# Revit family: SystemSchroeders_2flg.Tür
name_source: partatom
category: Türen
revit_build: Autodesk Revit 2018 (Build: 20170223_1515(x64)
units: mm (PartAtom-declared; Revit-internal decimal feet)

## family parameters
Basisbauteil = Wand
Beim Laden mit Abzugskörper schneiden = Nein
Gemeinsam genutzt = Nein
Immer vertikal = Ja
OmniClass-Nummer = 23.30.10.00
OmniClass-Titel = Doors
Raumberechnungspunkt = Nein

## types (11) — shared parameters
Analytische Konstruktion = <None>
Breite = 2000 mm
Breite Rahmen Sichtfenster = 55 mm
Breite Sichtfenster = 260 mm
Dicke = 69 mm  [stored 0.226378 ft]
Einbauhöhe Sichtfenster = 1500 mm  [stored 4.92126 ft]
FrameCompensate = Edelstahl
Funktion = Innen
Hbl = 260 mm
Hersteller = System Schröders
Höhe = 2000 mm
Höhe Sichtfenster = 260 mm
Höhe Türgriff = 1050 mm
Luftdichtigkeit = bis Klasse 3 (600 Pa)
PanelWidth = 1957 mm
Rahmenbreite = 22 mm
URL = https://www.system-schroeders.de
Wandabschluss = Nach Basisbauteil
Werkstoff Griff = Edelstahl
Werkstoff Rahmen = Edelstahl
Werkstoff Rahmen Sichtfenster = Edelstahl
Werkstoff Sichtfenster = Glas
Werkstoff Türblatt = Edelstahl
Wp_left = 979 mm
Wp_right = 974 mm
Öffnungswinkel = 90.00°

## per-type parameters (varying)
| type | Druck- / Sogwiderstand | Einbruchschutz | Feuerschutz | Rauchschutz | Schallschutz | Schlagregendichtheit | Widerstandsfähigkeit gegen Winlast |
| TSN-2 | 3800Pa | RC4 RC3 RC2 RC1 | T-30 | RS | 48 (-1;-5) dB |  |  |
| RSN-2 CE | 3800Pa | RC4 RC3 RC2 RC1 | - | RS | 48 (-1;-5) dB | bis Klasse 3A | bis Klasse C4 (2.000 Pa) |
| TSN-12 | 3800Pa | RC4 RC3 RC2 RC1 | T-90 | RS | 48 (-1;-5) dB |  |  |
| RSN-2 | 3800Pa | RC4 RC3 RC2 RC1 | - | RS | 48 (-1;-5) dB | bis Klasse 3A | bis Klasse C4 (2.000 Pa) |
| TSN-12 CE | 3800Pa | RC4 RC3 RC2 RC1 | EI2 90 -S a -C5 | S200 | 48 (-1;-5) dB | bis Klasse 3A | bis Klasse C4 (2.000 Pa) |
| ISN-2 | - | - | - | - | - | bis Klasse 3A | bis Klasse C4 (2.000 Pa) |
| TSN-2 CE | 3800Pa | RC4 RC3 RC2 RC1 | EI2 30 -S a -C5 | S200 | 48 (-1;-5) dB | bis Klasse 3A | bis Klasse C4 (2.000 Pa) |
| ASN-2 | 3800Pa | - | - | - | - | bis Klasse 3A | bis Klasse C4 (2.000 Pa) |
| TSN-4 CE | 3800Pa | RC4 RC3 RC2 RC1 | EI2 60 -S a -C5 | S200 | 48 (-1;-5) dB | bis Klasse 3A | bis Klasse C4 (2.000 Pa) |
| SN-2 | 3800Pa | - | - | - | 48 (-1;-5) dB | bis Klasse 3A | bis Klasse C4 (2.000 Pa) |
| ESN-2 | 3800Pa | RC4 RC3 RC2 RC1 | - | - | 48 (-1;-5) dB | bis Klasse 3A | bis Klasse C4 (2.000 Pa) |

note: [stored X ft] marks values corroborated as IEEE doubles in the binary element streams (Revit-internal decimal feet)

## geometry (parser evidence)
native form markers: Sweep x3
no freeform markers — native parametric forms only
